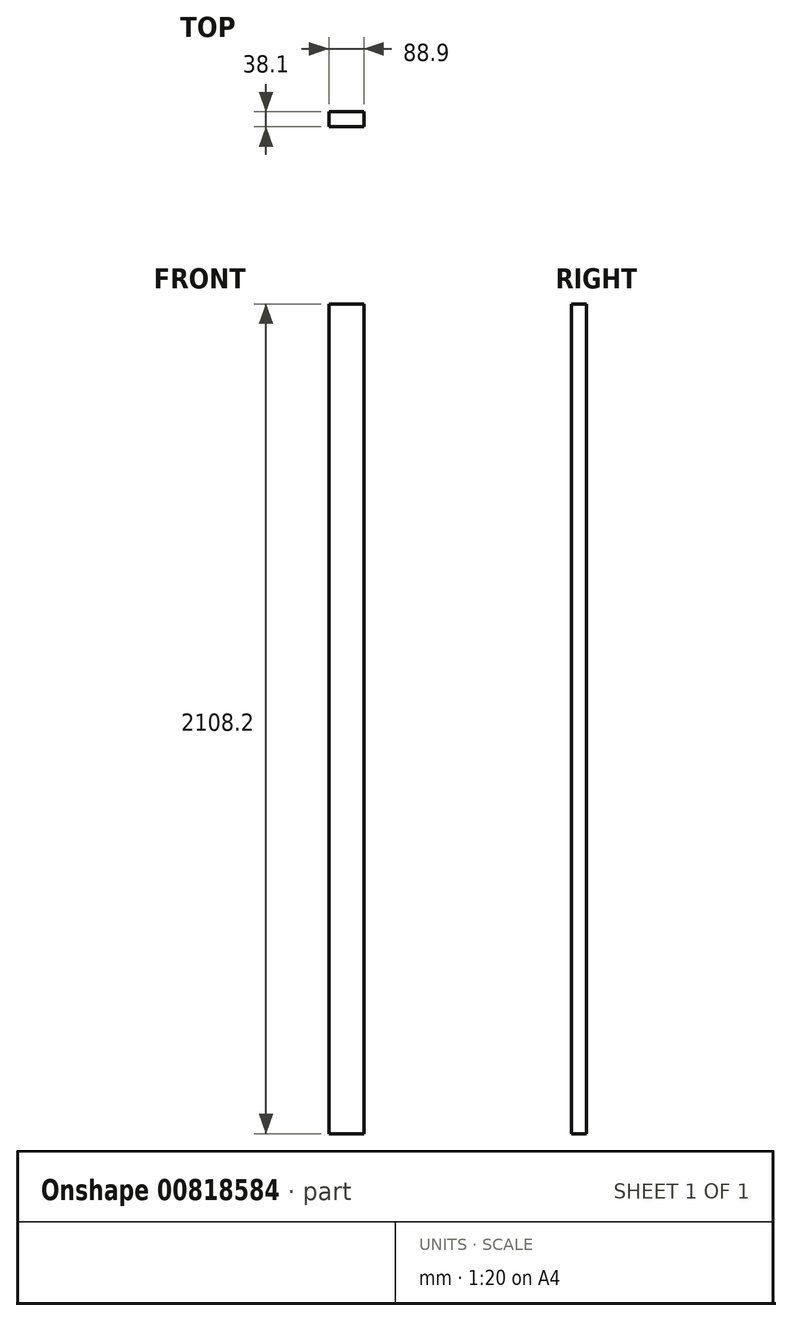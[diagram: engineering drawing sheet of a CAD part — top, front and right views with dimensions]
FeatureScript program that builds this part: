
annotation { "Feature Type Name" : "Feature", "Feature Type Description" : "" }
export const myFeature = defineFeature(function(context is Context, id is Id, definition is map)
    precondition{}
    {
        {
            var Q0;
            Q0=qCreatedBy(makeId("Top.planeOp"),FACE);
            var sketch = newSketch(context, id + "F0", { "sketchPlane" : qUnion([Q0])});
            skLineSegment(sketch, "E0.bottom", {"start": v(0, 0) * mm, "end": v(88.9, 0) * mm});
            skLineSegment(sketch, "E0.top", {"start": v(0, 38.1) * mm, "end": v(88.9, 38.1) * mm});
            skLineSegment(sketch, "E0.left", {"start": v(0, 0) * mm, "end": v(0, 38.1) * mm});
            skLineSegment(sketch, "E0.right", {"start": v(88.9, 0) * mm, "end": v(88.9, 38.1) * mm});
            skSolve(sketch);
        }
        {
            var Q0;
            Q0 = qSketchRegion(id + "F0", true);
            extrude(context, id + "F1", {"entities" : qUnion([Q0]), "depth" : 2108.2 * mm, "offsetDistance" : 25.4 * mm});
        }
    });
